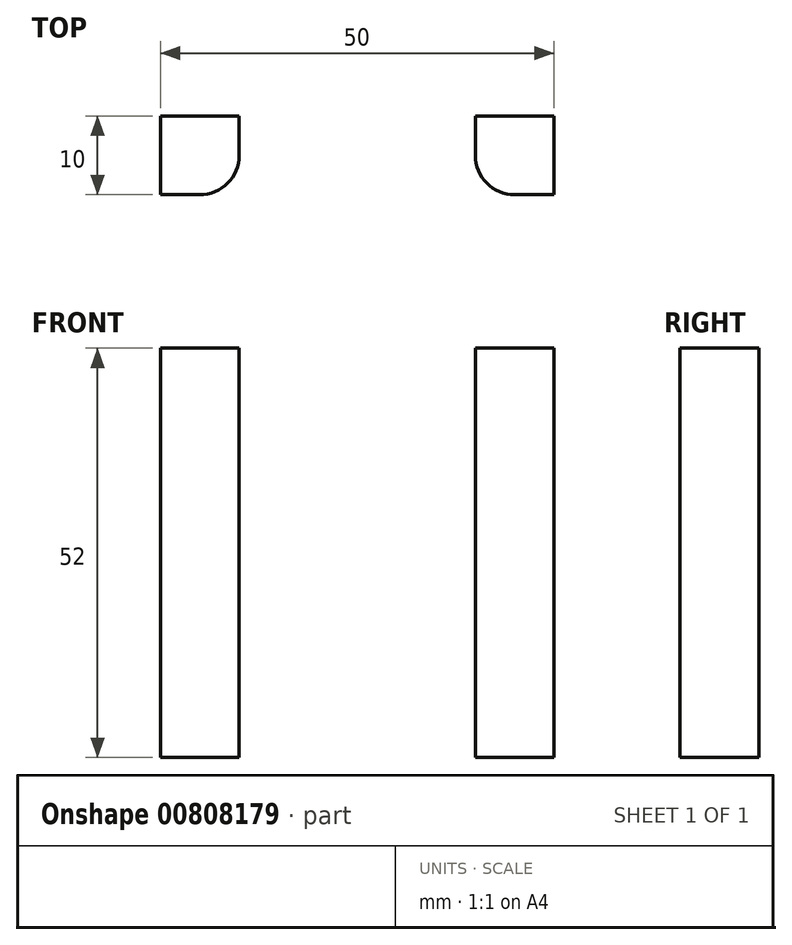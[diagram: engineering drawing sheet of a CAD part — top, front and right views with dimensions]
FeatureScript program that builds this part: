
annotation { "Feature Type Name" : "Feature", "Feature Type Description" : "" }
export const myFeature = defineFeature(function(context is Context, id is Id, definition is map)
    precondition{}
    {
        {
            var Q0;
            Q0=qCreatedBy(makeId("Top.planeOp"),FACE);
            var sketch = newSketch(context, id + "F0", { "sketchPlane" : qUnion([Q0])});
            skLineSegment(sketch, "E0.bottom", {"start": v(-25, 25) * mm, "end": v(25, 25) * mm});
            skLineSegment(sketch, "E0.top", {"start": v(-25, -25) * mm, "end": v(25, -25) * mm});
            skLineSegment(sketch, "E0.left", {"start": v(-25, 25) * mm, "end": v(-25, -25) * mm});
            skLineSegment(sketch, "E0.right", {"start": v(25, 25) * mm, "end": v(25, -25) * mm});
            skPoint(sketch, "E0.middle", {"position": v(0, 0) * mm});
            skLineSegment(sketch, "E1.bottom", {"start": v(-25, 25) * mm, "end": v(-15, 25) * mm});
            skLineSegment(sketch, "E1.top", {"start": v(-25, 15) * mm, "end": v(-15, 15) * mm});
            skLineSegment(sketch, "E1.left", {"start": v(-25, 25) * mm, "end": v(-25, 15) * mm});
            skLineSegment(sketch, "E1.right", {"start": v(-15, 25) * mm, "end": v(-15, 15) * mm});
            skLineSegment(sketch, "E2.bottom", {"start": v(-25, -25) * mm, "end": v(-15, -25) * mm});
            skLineSegment(sketch, "E2.top", {"start": v(-25, -15) * mm, "end": v(-15, -15) * mm});
            skLineSegment(sketch, "E2.left", {"start": v(-25, -25) * mm, "end": v(-25, -15) * mm});
            skLineSegment(sketch, "E2.right", {"start": v(-15, -25) * mm, "end": v(-15, -15) * mm});
            skLineSegment(sketch, "E3.bottom", {"start": v(25, -25) * mm, "end": v(15, -25) * mm});
            skLineSegment(sketch, "E3.top", {"start": v(25, -15) * mm, "end": v(15, -15) * mm});
            skLineSegment(sketch, "E3.left", {"start": v(25, -25) * mm, "end": v(25, -15) * mm});
            skLineSegment(sketch, "E3.right", {"start": v(15, -25) * mm, "end": v(15, -15) * mm});
            skLineSegment(sketch, "E4.bottom", {"start": v(25, 25) * mm, "end": v(15, 25) * mm});
            skLineSegment(sketch, "E4.top", {"start": v(25, 15) * mm, "end": v(15, 15) * mm});
            skLineSegment(sketch, "E4.left", {"start": v(25, 25) * mm, "end": v(25, 15) * mm});
            skLineSegment(sketch, "E4.right", {"start": v(15, 25) * mm, "end": v(15, 15) * mm});
            skPoint(sketch, "E5.visualSharp", {"position": v(-15, 15) * mm});
            skLineSegment(sketch, "E5.filletArc", {"start": v(-15, 15) * mm, "end": v(-15, 15) * mm});
            skPoint(sketch, "E6.visualSharp", {"position": v(-15, -15) * mm});
            skLineSegment(sketch, "E6.filletArc", {"start": v(-15, -15) * mm, "end": v(-15, -15) * mm});
            skPoint(sketch, "E7.visualSharp", {"position": v(15, -15) * mm});
            skLineSegment(sketch, "E7.filletArc", {"start": v(15, -15) * mm, "end": v(15, -15) * mm});
            skPoint(sketch, "E8.visualSharp", {"position": v(15, 15) * mm});
            skLineSegment(sketch, "E8.filletArc", {"start": v(15, 15) * mm, "end": v(15, 15) * mm});
            skSolve(sketch);
        }
        {
            var Q0;
            Q0=makeQuery(id+"F0.imprint","IMPRINT",FACE,{"disambiguationData":[TD([[makeQuery(id+"F0.imprint","IMPRINT",EDGE,{"derivedFrom":sQuery(id+"F0.wireOp",EDGE,"E0.bottom")}),-1.0]])]});
            extrude(context, id + "F1", {"entities" : qUnion([Q0]), "depth" : 52 * mm, "offsetDistance" : 25 * mm});
        }
        {
            var Q0;
            Q0=makeQuery(id+"F1.opExtrude","SWEPT_EDGE",EDGE,{"disambiguationData":[OSD([sQuery(id+"F0.wireOp",EDGE,"E2.top"),sQuery(id+"F0.wireOp",EDGE,"E2.right")])]});
            var Q1;
            Q1=makeQuery(id+"F1.opExtrude","SWEPT_EDGE",EDGE,{"disambiguationData":[OSD([sQuery(id+"F0.wireOp",EDGE,"E3.top"),sQuery(id+"F0.wireOp",EDGE,"E3.right")])]});
            var Q2;
            Q2=makeQuery(id+"F1.opExtrude","SWEPT_EDGE",EDGE,{"disambiguationData":[OSD([sQuery(id+"F0.wireOp",EDGE,"E4.top"),sQuery(id+"F0.wireOp",EDGE,"E4.right")])]});
            var Q3;
            Q3=makeQuery(id+"F1.opExtrude","SWEPT_EDGE",EDGE,{"disambiguationData":[OSD([sQuery(id+"F0.wireOp",EDGE,"E1.top"),sQuery(id+"F0.wireOp",EDGE,"E1.right")])]});
            fillet(context, id + "F2", {"entities" : qUnion([Q0, Q1, Q2, Q3]), "radius" : 5 * mm, "tangentPropagation" : true, "allowEdgeOverflow" : false});
        }
    });
